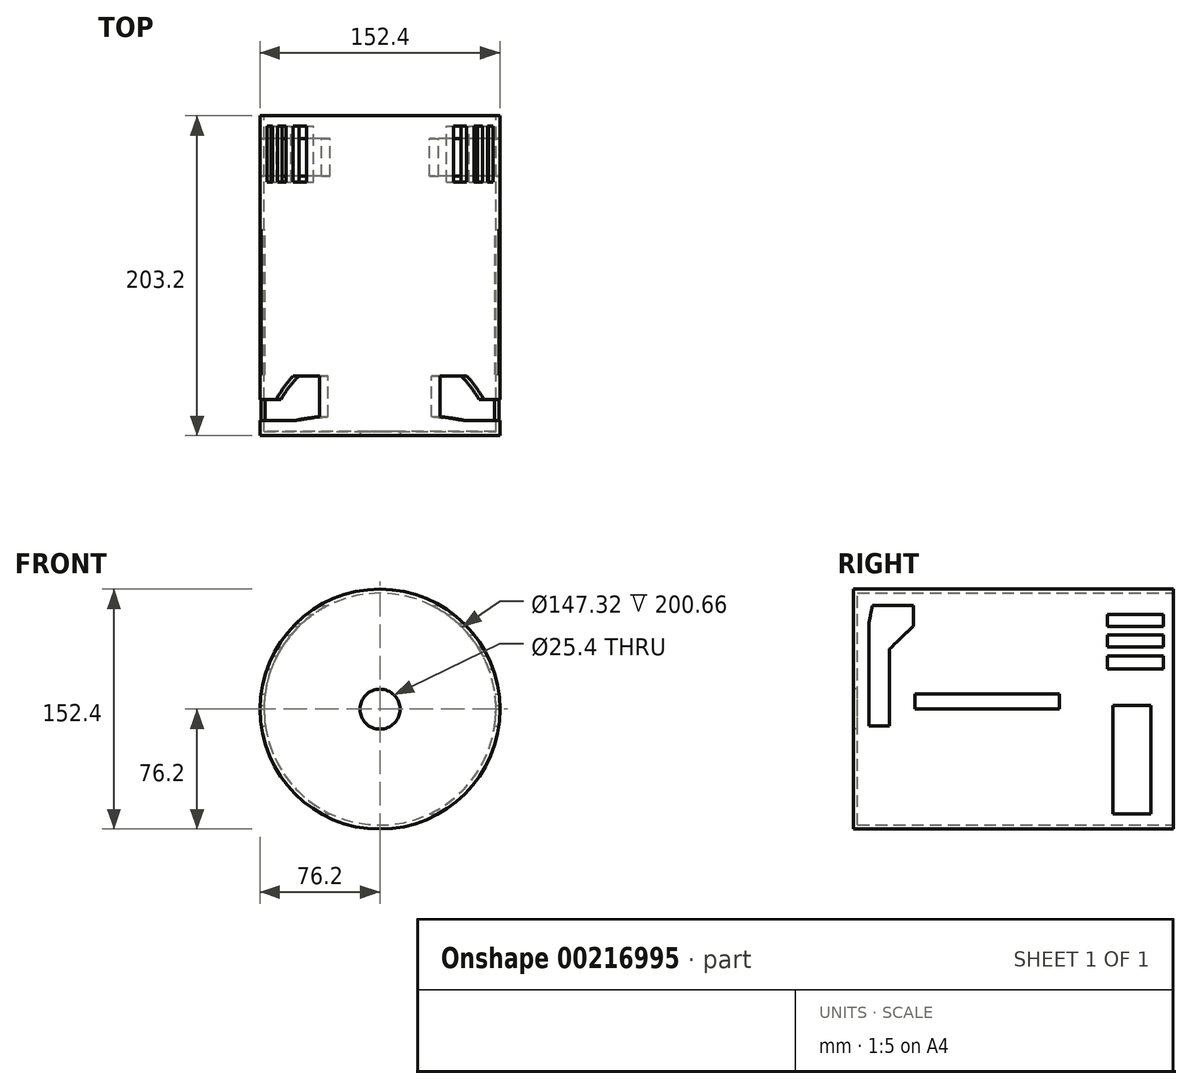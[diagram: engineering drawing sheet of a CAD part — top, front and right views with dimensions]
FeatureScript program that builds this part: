
annotation { "Feature Type Name" : "Feature", "Feature Type Description" : "" }
export const myFeature = defineFeature(function(context is Context, id is Id, definition is map)
    precondition{}
    {
        {
            var Q0;
            Q0=qCreatedBy(makeId("Front.planeOp"),FACE);
            var sketch = newSketch(context, id + "F0", { "sketchPlane" : qUnion([Q0])});
            skCircle(sketch, "E0", {"center": v(0, 0) * mm, "radius": 76.2 * mm});
            skSolve(sketch);
        }
        {
            var Q0;
            Q0 = qSketchRegion(id + "F0", true);
            extrude(context, id + "F1", {"entities" : qUnion([Q0]), "depth" : 203.2 * mm});
        }
        {
            var Q0;
            Q0=makeQuery(id+"F1.opExtrude","CAP_FACE",FACE,{"disambiguationData":[OSD([sQuery(id+"F0.wireOp",EDGE,"E0")])],"isStart":false});
            var sketch = newSketch(context, id + "F2", { "sketchPlane" : qUnion([Q0])});
            skCircle(sketch, "E1", {"center": v(0, 0) * mm, "radius": 12.7 * mm});
            skSolve(sketch);
        }
        {
            var Q0;
            Q0 = qSketchRegion(id + "F2", true);
            extrude(context, id + "F3", {"entities" : qUnion([Q0]), "operationType" : NewBodyOperationType.ADD, "depth" : 38.1 * mm});
        }
        {
            var Q0;
            Q0=makeQuery(id+"F1.opExtrude","CAP_FACE",FACE,{"disambiguationData":[OSD([sQuery(id+"F0.wireOp",EDGE,"E0")])],"isStart":true});
            shell(context, id + "F4", {"entities" : qUnion([Q0]), "thickness" : 2.54 * mm});
        }
        {
            var Q0;
            Q0=qCreatedBy(makeId("Right.planeOp"),FACE);
            var sketch = newSketch(context, id + "F5", { "sketchPlane" : qUnion([Q0])});
            skLineSegment(sketch, "E2", {"start": v(-191.12, 65.91) * mm, "end": v(-165.21, 65.91) * mm});
            skLineSegment(sketch, "E3", {"start": v(-165.21, 65.91) * mm, "end": v(-165.21, 52.67) * mm});
            skLineSegment(sketch, "E4", {"start": v(-165.21, 52.67) * mm, "end": v(-180.18, 38.28) * mm});
            skLineSegment(sketch, "E5", {"start": v(-180.18, 38.28) * mm, "end": v(-180.18, -10.65) * mm});
            skLineSegment(sketch, "E6", {"start": v(-180.18, -10.65) * mm, "end": v(-193.42, -10.65) * mm});
            skLineSegment(sketch, "E7", {"start": v(-193.42, -10.65) * mm, "end": v(-193.42, 54.4) * mm});
            skLineSegment(sketch, "E8", {"start": v(-193.42, 54.4) * mm, "end": v(-191.12, 65.91) * mm});
            skLineSegment(sketch, "E9.bottom", {"start": v(-6.46, 52.67) * mm, "end": v(-42.02, 52.67) * mm});
            skLineSegment(sketch, "E9.top", {"start": v(-6.46, 60.3) * mm, "end": v(-42.02, 60.3) * mm});
            skLineSegment(sketch, "E9.left", {"start": v(-6.46, 52.67) * mm, "end": v(-6.46, 60.3) * mm});
            skLineSegment(sketch, "E9.right", {"start": v(-42.02, 52.67) * mm, "end": v(-42.02, 60.3) * mm});
            skPoint(sketch, "E9.middle", {"position": v(-24.24, 56.48) * mm});
            skLineSegment(sketch, "E10.bottom", {"start": v(-6.46, 39.65) * mm, "end": v(-42.02, 39.65) * mm});
            skLineSegment(sketch, "E10.top", {"start": v(-6.46, 47.27) * mm, "end": v(-42.02, 47.27) * mm});
            skLineSegment(sketch, "E10.left", {"start": v(-6.46, 39.65) * mm, "end": v(-6.46, 47.27) * mm});
            skLineSegment(sketch, "E10.right", {"start": v(-42.02, 39.65) * mm, "end": v(-42.02, 47.27) * mm});
            skPoint(sketch, "E10.middle", {"position": v(-24.24, 43.46) * mm});
            skLineSegment(sketch, "E11.bottom", {"start": v(-6.46, 25.62) * mm, "end": v(-42.02, 25.62) * mm});
            skLineSegment(sketch, "E11.top", {"start": v(-6.46, 33.68) * mm, "end": v(-42.02, 33.68) * mm});
            skLineSegment(sketch, "E11.left", {"start": v(-6.46, 25.62) * mm, "end": v(-6.46, 33.68) * mm});
            skLineSegment(sketch, "E11.right", {"start": v(-42.02, 25.62) * mm, "end": v(-42.02, 33.68) * mm});
            skPoint(sketch, "E11.middle", {"position": v(-24.24, 29.65) * mm});
            skSolve(sketch);
        }
        {
            var Q0;
            Q0=makeQuery(id+"F5.imprint","IMPRINT",FACE,{"disambiguationData":[TD([[makeQuery(id+"F5.imprint","IMPRINT",EDGE,{"derivedFrom":sQuery(id+"F5.wireOp",EDGE,"E9.bottom")}),-1.0]])]});
            var Q1;
            Q1=makeQuery(id+"F5.imprint","IMPRINT",FACE,{"disambiguationData":[TD([[makeQuery(id+"F5.imprint","IMPRINT",EDGE,{"derivedFrom":sQuery(id+"F5.wireOp",EDGE,"E10.bottom")}),-1.0]])]});
            var Q2;
            Q2=makeQuery(id+"F5.imprint","IMPRINT",FACE,{"disambiguationData":[TD([[makeQuery(id+"F5.imprint","IMPRINT",EDGE,{"derivedFrom":sQuery(id+"F5.wireOp",EDGE,"E11.bottom")}),-1.0]])]});
            var Q3;
            Q3=makeQuery(id+"F5.imprint","IMPRINT",FACE,{"disambiguationData":[TD([[makeQuery(id+"F5.imprint","IMPRINT",EDGE,{"derivedFrom":sQuery(id+"F5.wireOp",EDGE,"E2")}),-1.0]])]});
            extrude(context, id + "F6", {"entities" : qUnion([Q0, Q1, Q2, Q3]), "operationType" : NewBodyOperationType.REMOVE, "oppositeDirection" : true, "depth" : 177.8 * mm, "symmetric" : true});
        }
        {
            var Q0;
            Q0=makeQuery(id+"F3.opExtrude","CAP_FACE",FACE,{"disambiguationData":[OSD([sQuery(id+"F2.wireOp",EDGE,"E1")])],"isStart":false});
            var sketch = newSketch(context, id + "F7", { "sketchPlane" : qUnion([Q0])});
            skSolve(sketch);
        }
        {
            var Q0;
            Q0=makeQuery(id+"F7.imprint","IMPRINT",FACE,{"disambiguationData":[TD([[makeQuery(id+"F7.imprint","IMPRINT",EDGE,{"derivedFrom":makeQuery(id+"F3.opExtrude","CAP_EDGE",EDGE,{"disambiguationData":[OSD([sQuery(id+"F2.wireOp",EDGE,"E1")])],"isStart":false})}),1.0]])]});
            extrude(context, id + "F8", {"entities" : qUnion([Q0]), "operationType" : NewBodyOperationType.REMOVE, "endBound" : BoundingType.THROUGH_ALL, "oppositeDirection" : true, "depth" : 25.4 * mm});
        }
        {
            var Q0;
            Q0=qCreatedBy(makeId("Right.planeOp"),FACE);
            var sketch = newSketch(context, id + "F9", { "sketchPlane" : qUnion([Q0])});
            skLineSegment(sketch, "E12.bottom", {"start": v(-14.34, -66.53) * mm, "end": v(-38.38, -66.53) * mm});
            skLineSegment(sketch, "E12.top", {"start": v(-14.34, 2.4) * mm, "end": v(-38.38, 2.4) * mm});
            skLineSegment(sketch, "E12.left", {"start": v(-14.34, -66.53) * mm, "end": v(-14.34, 2.4) * mm});
            skLineSegment(sketch, "E12.right", {"start": v(-38.38, -66.53) * mm, "end": v(-38.38, 2.4) * mm});
            skPoint(sketch, "E12.middle", {"position": v(-26.36, -32.07) * mm});
            skLineSegment(sketch, "E13.bottom", {"start": v(-72.32, 0) * mm, "end": v(-164.23, 0) * mm});
            skLineSegment(sketch, "E13.top", {"start": v(-72.32, 9.61) * mm, "end": v(-164.23, 9.61) * mm});
            skLineSegment(sketch, "E13.left", {"start": v(-72.32, 0) * mm, "end": v(-72.32, 9.61) * mm});
            skLineSegment(sketch, "E13.right", {"start": v(-164.23, 0) * mm, "end": v(-164.23, 9.61) * mm});
            skPoint(sketch, "E13.middle", {"position": v(-118.27, 4.8) * mm});
            skSolve(sketch);
        }
        {
            var Q0;
            Q0 = qSketchRegion(id + "F9", true);
            extrude(context, id + "F10", {"entities" : qUnion([Q0]), "operationType" : NewBodyOperationType.REMOVE, "oppositeDirection" : true, "depth" : 254 * mm, "symmetric" : true});
        }
    });
